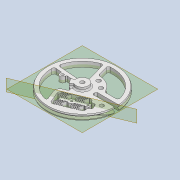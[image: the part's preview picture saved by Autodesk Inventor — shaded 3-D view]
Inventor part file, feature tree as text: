
AUTODESK INVENTOR PART (.ipt)
format: ipt  version: 2020 (Build 240168000, 168)  size: 1,932,288 bytes
history: native  units: mm
features: sketch x23, extrude x22, projected_geometry x20, fillet x15, thicken_offset x10, chamfer x5, other x4, pattern_linear x2, plane x2, reference x2, revolve x1, mirror x1
ambient origin geometry x8: Origin, YZ Plane, XZ Plane, XY Plane, X Axis, Y Axis, Z Axis, Center Point
bodies: Solid1 (feature_tree)
feature tree (107):
  extrude  "Extrusion1"  Depth=3.0mm TaperAngle=0.0deg
  revolve  "Revolution1"  [1 undecoded]
  extrude  "Extrusion2"  Depth=6.0mm
  extrude  "Extrusion3"  Depth=11.0mm
  extrude  "Extrusion4"  Depth=34.0mm
  extrude  "Extrusion5"  Depth=14.0mm
  chamfer  "Chamfer1"  Distance=5.0mm
  fillet  "Fillet1"  Radius=2.5mm
  fillet  "Fillet2"  Radius=15.0mm
  extrude  "Extrusion6"  Depth=0.5mm
  extrude  "Extrusion7"  TaperAngle=45.0deg  [1 undecoded]
  extrude  "Extrusion8"  Depth=12.0mm
  pattern_linear  "Rectangular Pattern1"  Count1=2  [1 undecoded]
  pattern_linear  "Rectangular Pattern2"  Spacing1=3.0mm  [1 undecoded]
  thicken_offset  "Thicken1"
  chamfer  "Chamfer2"  Distance=40.0mm
  plane  "Work Plane1"
  mirror  "Mirror1"
  extrude  "Extrusion9"  Depth=10.0mm
  fillet  "Fillet3"  Radius=1.0mm
  fillet  "Fillet4"  Radius=1.0mm
  fillet  "Fillet5"  Radius=1.0mm
  fillet  "Fillet6"  Radius=5.0mm
  extrude  "Extrusion10"  Depth=4.0mm
  fillet  "Fillet7"  Radius=3.0mm
  chamfer  "Chamfer3"  Distance=2.0mm
  extrude  "Extrusion11"  Depth=2.0mm
  fillet  "Fillet8"  Radius=1.0mm
  thicken_offset  "Thicken2"
  fillet  "Fillet9"  Radius=0.5mm
  extrude  "Extrusion12"  Depth=1.5mm
  thicken_offset  "Thicken3"
  thicken_offset  "Thicken4"
  chamfer  "Chamfer4"  Distance=3.0mm
  plane  "Work Plane2"
  extrude  "Extrusion13"  Depth=2.0mm
  chamfer  "Chamfer5"  Distance=3.0mm
  extrude  "Extrusion14"  Depth=2.0mm
  extrude  "Extrusion15"  Depth=0.5mm TaperAngle=45.0deg
  fillet  "Fillet10"  Radius=1.5mm
  fillet  "Fillet11"  Radius=1.4mm
  fillet  "Fillet12"  Radius=1.4mm
  thicken_offset  "Thicken5"
  thicken_offset  "Thicken6"
  thicken_offset  "Thicken7"
  extrude  "Extrusion16"  Depth=2.0mm TaperAngle=0.0deg
  extrude  "Extrusion17"  Depth=1.0mm
  extrude  "Extrusion18"  Depth=2.0mm
  extrude  "Extrusion19"  Depth=2.0mm
  thicken_offset  "Thicken8"
  thicken_offset  "Thicken9"
  extrude  "Extrusion20"  Depth=0.5mm
  fillet  "Fillet13"  Radius=7.3mm
  fillet  "Fillet14"  Radius=7.330383mm
  extrude  "Extrusion21"  Depth=2.0mm
  extrude  "Extrusion22"  Depth=2.0mm TaperAngle=0.0deg
  fillet  "Fillet16"  Radius=0.5mm
  thicken_offset  "Thicken10"
  sketch  "Sketch1"  dims[d0=50.0mm d1=3.0mm d2=0.0mm]
  sketch  "Sketch2"  dims[d3=1.5mm d4=1.5mm]
  projected_geometry  "Projected Loop1"
  sketch  "Sketch3"  dims[d5=90.0deg d6=6.0mm]
  sketch  "Sketch4"  dims[d7=3.0mm d8=0.0mm d9=11.0mm]
  projected_geometry  "Projected Loop2"
  sketch  "Sketch5"  dims[d10=5.0mm d11=0.0mm d12=34.0mm]
  projected_geometry  "Projected Loop3"
  sketch  "Sketch6"  dims[d13=3.0mm d14=14.0mm d15=5.0mm d16=0.0mm d17=2.5mm d18=15.0mm d19=0.0mm]
  projected_geometry  "Projected Loop4"
  sketch  "Sketch7"  dims[d20=0.5mm d21=2.0mm d22=45.0deg d23=0.5mm]
  projected_geometry  "Projected Loop5"
  sketch  "Sketch8"  dims[d24=1.0mm d25=45.0deg]
  projected_geometry  "Projected Loop6"
  sketch  "Sketch9"  dims[d26=3.0mm d27=12.0mm d28=20.0mm]
  projected_geometry  "Projected Loop7"
  projected_geometry  "Projected Loop8"
  sketch  "Sketch10"  dims[d29=15.0mm d30=0.0mm]
  projected_geometry  "Projected Loop9"
  sketch  "Sketch11"  dims[d31=4.0mm]
  projected_geometry  "Projected Loop10"
  sketch  "Sketch12"  dims[d32=4.0mm]
  projected_geometry  "Projected Loop11"
  sketch  "Sketch13"  dims[d33=2.0mm]
  projected_geometry  "Projected Loop12"
  sketch  "Sketch14"  dims[d34=14.0mm]
  reference  "Reference1"
  sketch  "Sketch15"  dims[d35=3.0mm d36=0.0mm]
  projected_geometry  "Projected Loop13"
  sketch  "Sketch16"  dims[d37=3.0mm]
  projected_geometry  "Projected Loop14"
  sketch  "Sketch17"  dims[d38=0.5mm]
  sketch  "Sketch18"  dims[d39=0.5mm]
  sketch  "Sketch19"  dims[d40=2.2mm]
  projected_geometry  "Projected Loop15"
  projected_geometry  "Projected Loop16"
  sketch  "Sketch20"  dims[d41=3.5mm]
  projected_geometry  "Projected Loop17"
  sketch  "Sketch21"  dims[d42=0.5mm]
  projected_geometry  "Projected Loop18"
  sketch  "Sketch22"  dims[d43=3.5mm]
  projected_geometry  "Projected Loop19"
  reference  "Reference2"
  sketch  "Sketch23"  dims[d44=0.5mm d45=3.0mm d46=0.0mm d47=40.0mm d49=1.3mm d50=20.0mm d52=10.0mm d53=1.0mm d54=1.0mm d55=1.0mm d56=2.0mm d57=45.0deg d58=5.0mm d59=4.0mm d60=3.0mm d61=0.0mm d62=2.0mm d63=2.0mm d64=1.0mm d65=0.5mm d66=1.5mm d67=3.0mm d68=3.0mm d69=3.0mm d70=0.0mm d71=0.2mm d72=0.5mm d73=2.0mm d74=45.0deg d75=1.5mm d76=1.4mm d77=1.4mm d78=3.0mm d79=0.0mm d80=1.0mm d81=5.0mm d82=5.0mm d83=0.5mm d84=7.3mm d85=7.330383mm d86=3.0mm d87=3.0mm d88=0.0mm d89=0.5mm d90=0.5mm d91=0.5mm d92=0.5mm d93=0.5mm d94=2.0mm d95=45.0deg d96=-2.0mm d97=1.0mm d98=4.5mm d99=0.0mm d100=1.0mm d101=2.0mm d102=45.0deg d103=6.108652mm d104=6.981317mm d105=10.0mm d106=3.1mm d107=10.0mm d108=3.1mm d109=4.5mm d110=0.0mm d111=18.0mm d112=46.0mm d113=2.5mm d114=2.5mm d115=2.5mm d116=2.5mm d117=26.0mm d118=3.0mm d119=4.712389mm d120=12.217305mm d121=4.5mm d122=0.0mm d123=4.0mm d124=1.0mm d125=1.5mm d126=2.0mm d127=2.0mm d128=2.0mm d129=2.0mm d130=1.0mm d131=1.0mm d132=4.5mm d133=0.0mm d134=3.0mm d135=4.5mm d136=0.0mm d137=12.0mm d138=25.481807mm d139=4.0mm d140=4.5mm d141=0.0mm d142=4.5mm d143=0.0mm d144=1.0mm d145=1.0mm d146=1.0mm d147=1.0mm d148=4.0mm d149=1.4mm d150=6.0mm d151=0.0mm d152=1.0mm d153=1.0mm d158=2.3mm d159=4.0mm d160=4.0mm d161=0.0mm d162=2.0mm d163=4.0mm d164=0.0mm d165=0.5mm d166=2.0mm d167=2.0mm]
  projected_geometry  "Projected Loop20"
  parser-record x1  (decoder bookkeeping rows leaked as tree rows — omitted from the tree; the rows remain in map.json)
  other  "driver_ass_1.iam"
  other  "bearing_3_6_2:1"
  other  "driver_wheel_1:1"
note: 4 required parameter values undecoded (feature->parameter linkage not recoverable at this tier; creation-order binding heuristic only, values carry confidence <= 0.55)
note: 1 file-system path scrubbed to <path> (originals preserved in map.json)